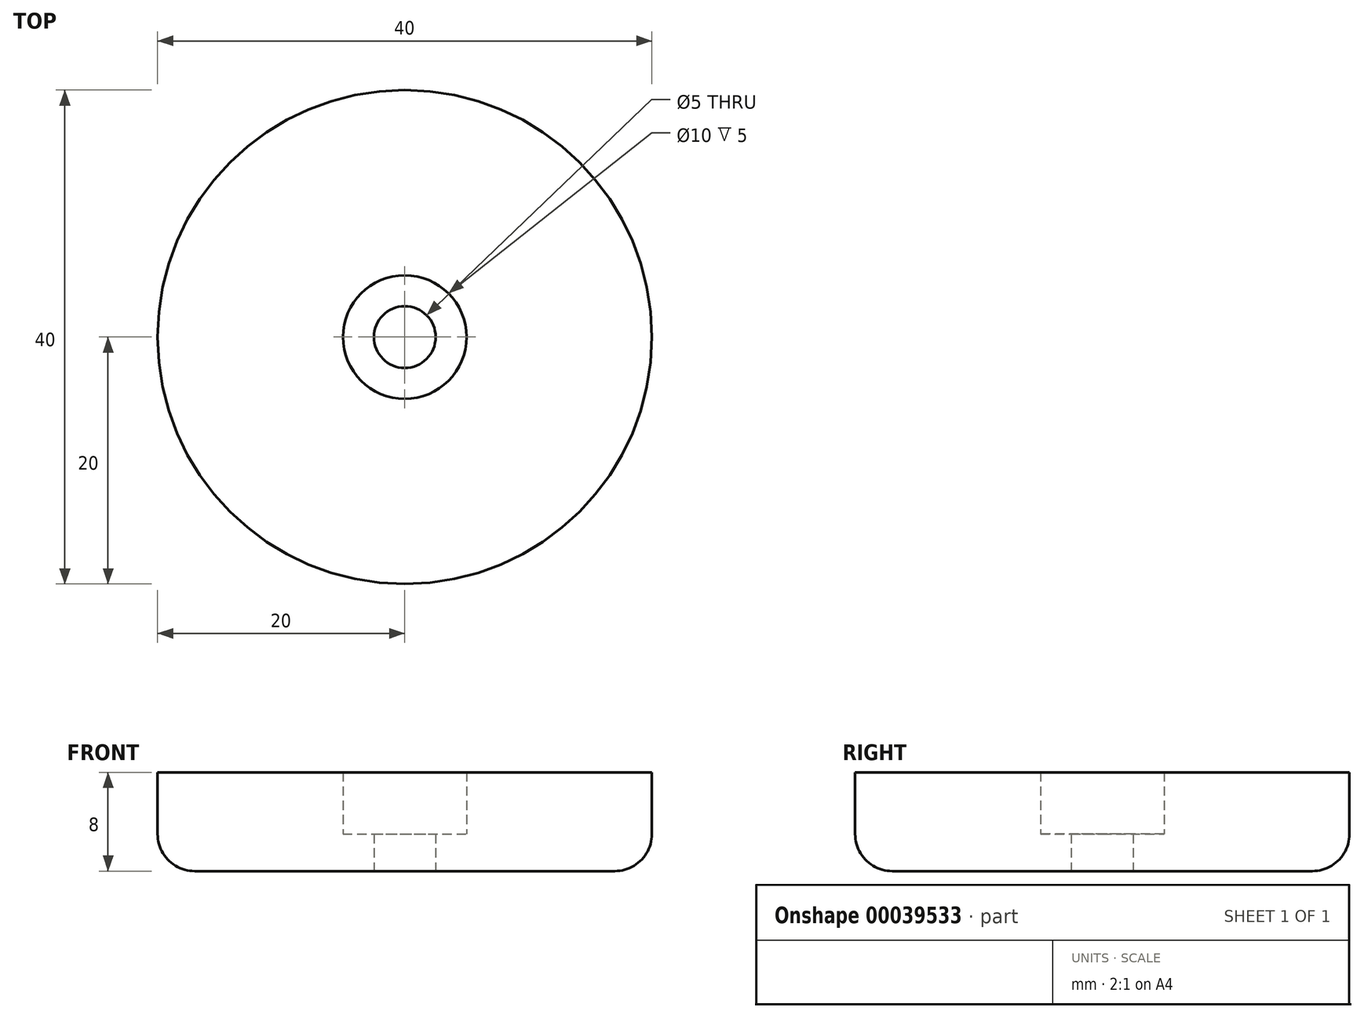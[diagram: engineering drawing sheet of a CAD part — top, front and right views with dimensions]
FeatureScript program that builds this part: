
annotation { "Feature Type Name" : "Feature", "Feature Type Description" : "" }
export const myFeature = defineFeature(function(context is Context, id is Id, definition is map)
    precondition{}
    {
        {
            var Q0;
            Q0=qCreatedBy(makeId("Top.planeOp"),FACE);
            var sketch = newSketch(context, id + "F0", { "sketchPlane" : qUnion([Q0])});
            skCircle(sketch, "E0", {"center": v(0, 0) * mm, "radius": 20 * mm});
            skSolve(sketch);
        }
        {
            var Q0;
            Q0=qSketchRegion(id+"F0",true);
            extrude(context, id + "F1", {"entities" : qUnion([Q0]), "depth" : 8 * mm});
        }
        {
            var Q0;
            Q0=makeQuery(id+"F1.opExtrude","CAP_FACE",FACE,{"disambiguationData":[OSD([sQuery(id+"F0.wireOp",EDGE,"E0")])],"isStart":false});
            var sketch = newSketch(context, id + "F2", { "sketchPlane" : qUnion([Q0])});
            skCircle(sketch, "E1", {"center": v(0, 0) * mm, "radius": 19 * mm});
            skSolve(sketch);
        }
        {
            var Q0;
            Q0=makeQuery(id+"F1.opExtrude","CAP_EDGE",EDGE,{"disambiguationData":[OSD([sQuery(id+"F0.wireOp",EDGE,"E0")])],"isStart":true});
            fillet(context, id + "F3", {"entities" : qUnion([Q0]), "radius" : 3 * mm, "tangentPropagation" : true, "allowEdgeOverflow" : false});
        }
        {
            var Q0;
            Q0=makeQuery(id+"F2.imprint","IMPRINT",FACE,{"disambiguationData":[TD([[makeQuery(id+"F2.imprint","IMPRINT",EDGE,{"derivedFrom":sQuery(id+"F2.wireOp",EDGE,"E1")}),1.0]])]});
            var sketch = newSketch(context, id + "F4", { "sketchPlane" : qUnion([Q0])});
            skCircle(sketch, "E2", {"center": v(0, 0) * mm, "radius": 4 * mm});
            skSolve(sketch);
        }
        {
            var Q0;
            Q0=sQuery(id+"F4.wireOp",VERTEX,"E2.center");
            var Q1;
            Q1=makeQuery(id+"F1.opExtrude","SWEPT_BODY",BODY,{"disambiguationData":[OSD([sQuery(id+"F0.wireOp",EDGE,"E0")])]});
            hole(context, id + "F5", {"style" : HoleStyle.C_BORE, "holeDiameter" : 5 * mm, "cBoreDiameter" : 10 * mm, "cBoreDepth" : 5 * mm, "endStyle" : HoleEndStyle.THROUGH, "locations" : qUnion([Q0]), "scope" : qUnion([Q1])});
        }
    });
